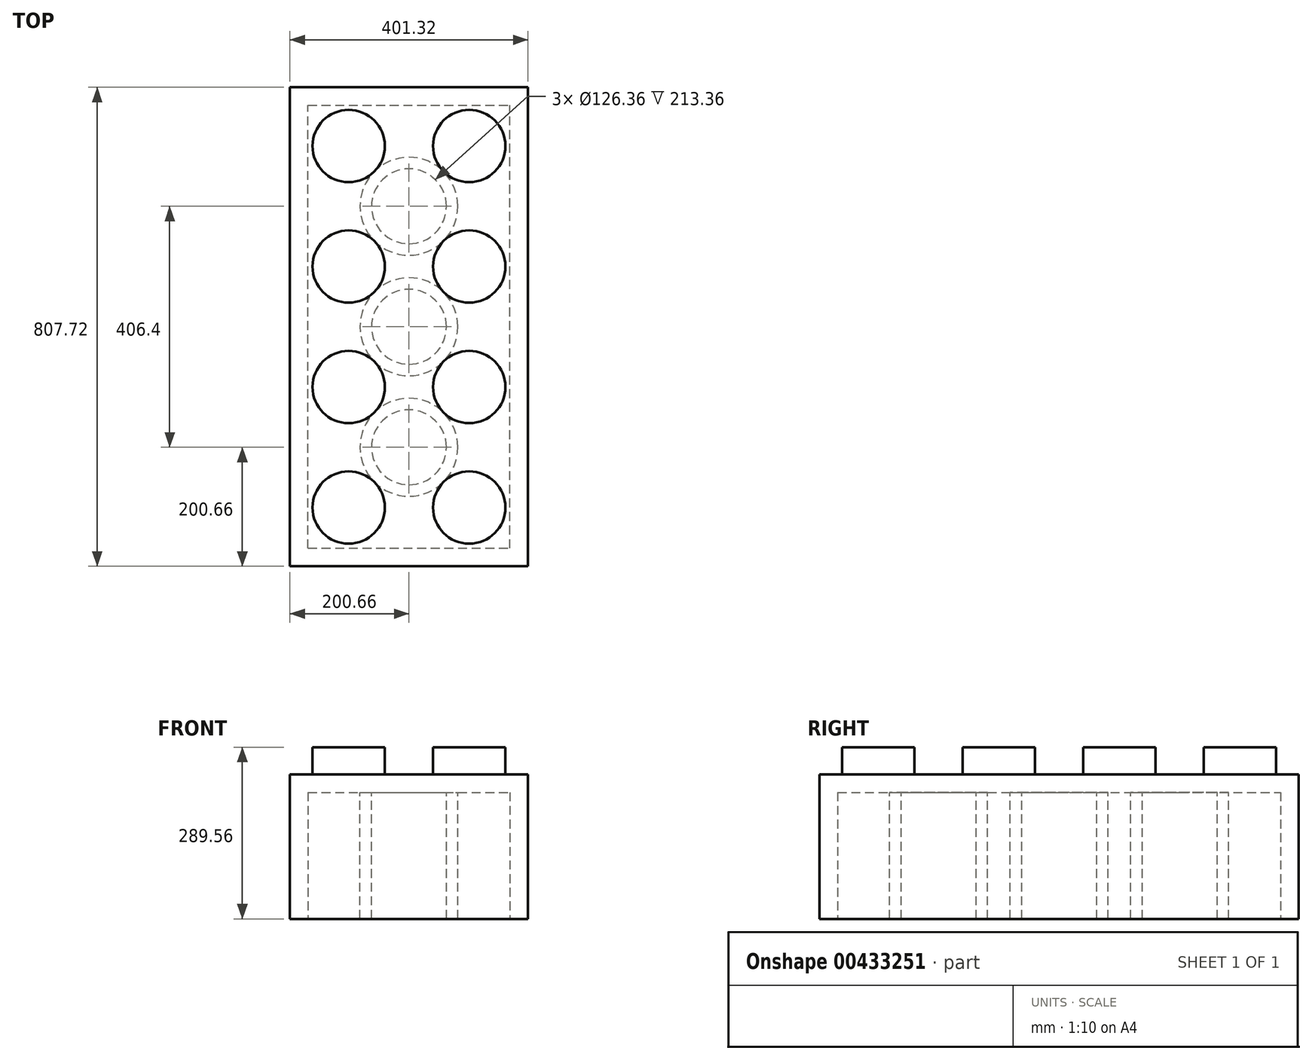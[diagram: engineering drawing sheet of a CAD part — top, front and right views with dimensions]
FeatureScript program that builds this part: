
annotation { "Feature Type Name" : "Feature", "Feature Type Description" : "" }
export const myFeature = defineFeature(function(context is Context, id is Id, definition is map)
    precondition{}
    {
        {
            var Q0;
            Q0=qCreatedBy(makeId("Top.planeOp"),FACE);
            var sketch = newSketch(context, id + "F0", { "sketchPlane" : qUnion([Q0])});
            skLineSegment(sketch, "E0.bottom", {"start": v(-200.66, -403.86) * mm, "end": v(200.66, -403.86) * mm});
            skLineSegment(sketch, "E0.top", {"start": v(-200.66, 403.86) * mm, "end": v(200.66, 403.86) * mm});
            skLineSegment(sketch, "E0.left", {"start": v(-200.66, -403.86) * mm, "end": v(-200.66, 403.86) * mm});
            skLineSegment(sketch, "E0.right", {"start": v(200.66, -403.86) * mm, "end": v(200.66, 403.86) * mm});
            skPoint(sketch, "E0.middle", {"position": v(0, 0) * mm});
            skSolve(sketch);
        }
        {
            var Q0;
            Q0=qSketchRegion(id+"F0",true);
            extrude(context, id + "F1", {"entities" : qUnion([Q0]), "depth" : 243.84 * mm});
        }
        {
            var Q0;
            Q0=makeQuery(id+"F1.opExtrude","CAP_FACE",FACE,{"disambiguationData":[OSD([sQuery(id+"F0.wireOp",EDGE,"E0.bottom"),sQuery(id+"F0.wireOp",EDGE,"E0.top"),sQuery(id+"F0.wireOp",EDGE,"E0.left"),sQuery(id+"F0.wireOp",EDGE,"E0.right")])],"isStart":false});
            var sketch = newSketch(context, id + "F2", { "sketchPlane" : qUnion([Q0])});
            skCircle(sketch, "E1", {"center": v(101.6, 304.8) * mm, "radius": 60.96 * mm});
            skCircle(sketch, "E2.0.1.0", {"center": v(101.6, 101.6) * mm, "radius": 60.96 * mm});
            skCircle(sketch, "E2.0.2.0", {"center": v(101.6, -101.6) * mm, "radius": 60.96 * mm});
            skCircle(sketch, "E2.0.3.0", {"center": v(101.6, -304.8) * mm, "radius": 60.96 * mm});
            skCircle(sketch, "E2.1.0.0", {"center": v(-101.6, 304.8) * mm, "radius": 60.96 * mm});
            skCircle(sketch, "E2.1.1.0", {"center": v(-101.6, 101.6) * mm, "radius": 60.96 * mm});
            skCircle(sketch, "E2.1.2.0", {"center": v(-101.6, -101.6) * mm, "radius": 60.96 * mm});
            skCircle(sketch, "E2.1.3.0", {"center": v(-101.6, -304.8) * mm, "radius": 60.96 * mm});
            skLineSegment(sketch, "E2.direction1", {"start": v(101.6, 304.8) * mm, "end": v(-101.6, 304.8) * mm, "construction": true});
            skLineSegment(sketch, "E2.direction2", {"start": v(101.6, 304.8) * mm, "end": v(101.6, 101.6) * mm, "construction": true});
            skSolve(sketch);
        }
        {
            var Q0;
            Q0=qSketchRegion(id+"F2",true);
            extrude(context, id + "F3", {"entities" : qUnion([Q0]), "operationType" : NewBodyOperationType.ADD, "depth" : 45.72 * mm});
        }
        {
            var Q0;
            Q0=makeQuery(id+"F1.opExtrude","CAP_FACE",FACE,{"disambiguationData":[OSD([sQuery(id+"F0.wireOp",EDGE,"E0.bottom"),sQuery(id+"F0.wireOp",EDGE,"E0.top"),sQuery(id+"F0.wireOp",EDGE,"E0.left"),sQuery(id+"F0.wireOp",EDGE,"E0.right")])],"isStart":true});
            var sketch = newSketch(context, id + "F4", { "sketchPlane" : qUnion([Q0])});
            skLineSegment(sketch, "E3.bottom", {"start": v(-170.18, 373.38) * mm, "end": v(170.18, 373.38) * mm});
            skLineSegment(sketch, "E3.top", {"start": v(-170.18, -373.38) * mm, "end": v(170.18, -373.38) * mm});
            skLineSegment(sketch, "E3.left", {"start": v(-170.18, 373.38) * mm, "end": v(-170.18, -373.38) * mm});
            skLineSegment(sketch, "E3.right", {"start": v(170.18, 373.38) * mm, "end": v(170.18, -373.38) * mm});
            skPoint(sketch, "E3.middle", {"position": v(0, 0) * mm});
            skSolve(sketch);
        }
        {
            var Q0;
            Q0=makeQuery(id+"F4.imprint","IMPRINT",FACE,{"disambiguationData":[TD([[makeQuery(id+"F4.imprint","IMPRINT",EDGE,{"derivedFrom":sQuery(id+"F4.wireOp",EDGE,"E3.bottom")}),-1.0]])]});
            extrude(context, id + "F5", {"entities" : qUnion([Q0]), "operationType" : NewBodyOperationType.REMOVE, "oppositeDirection" : true, "depth" : 213.36 * mm});
        }
        {
            var Q0;
            Q0=makeQuery(id+"F5.boolean.opBoolean","COPY",FACE,{"derivedFrom":makeQuery(id+"F5.opExtrude","CAP_FACE",FACE,{"disambiguationData":[OSD([sQuery(id+"F4.wireOp",EDGE,"E3.bottom"),sQuery(id+"F4.wireOp",EDGE,"E3.top"),sQuery(id+"F4.wireOp",EDGE,"E3.left"),sQuery(id+"F4.wireOp",EDGE,"E3.right")])],"isStart":false})});
            var sketch = newSketch(context, id + "F6", { "sketchPlane" : qUnion([Q0])});
            skCircle(sketch, "E4", {"center": v(0, 0) * mm, "radius": 82.55 * mm});
            skCircle(sketch, "E5", {"center": v(0, 0) * mm, "radius": 63.18 * mm});
            skCircle(sketch, "E6.0.1.0", {"center": v(0, 203.2) * mm, "radius": 82.55 * mm});
            skLineSegment(sketch, "E6.direction1", {"start": v(0, 0) * mm, "end": v(25.4, 0) * mm, "construction": true});
            skLineSegment(sketch, "E6.direction2", {"start": v(0, 0) * mm, "end": v(0, 203.2) * mm, "construction": true});
            skCircle(sketch, "E7.0.1.0", {"center": v(0, 203.2) * mm, "radius": 63.18 * mm});
            skCircle(sketch, "E8.0.1.0", {"center": v(0, -203.2) * mm, "radius": 63.18 * mm});
            skCircle(sketch, "E8.0.1.1", {"center": v(0, -203.2) * mm, "radius": 82.55 * mm});
            skLineSegment(sketch, "E8.direction1", {"start": v(0, 203.2) * mm, "end": v(25.4, 203.2) * mm, "construction": true});
            skLineSegment(sketch, "E8.direction2", {"start": v(0, 203.2) * mm, "end": v(0, -203.2) * mm, "construction": true});
            skSolve(sketch);
        }
        {
            var Q0;
            Q0=qSketchRegion(id+"F6",true);
            var Q1;
            Q1=sQuery(id+"F6.wireOp",EDGE,"E6.0.1.0");
            var Q2;
            Q2=sQuery(id+"F6.wireOp",EDGE,"E7.0.1.0");
            var Q3;
            Q3=sQuery(id+"F6.wireOp",EDGE,"E5");
            var Q4;
            Q4=sQuery(id+"F6.wireOp",EDGE,"E4");
            var Q5;
            Q5=sQuery(id+"F6.wireOp",EDGE,"E8.0.1.0");
            var Q6;
            Q6=sQuery(id+"F6.wireOp",EDGE,"E8.0.1.1");
            extrude(context, id + "F7", {"entities" : qUnion([Q0]), "operationType" : NewBodyOperationType.ADD, "surfaceEntities" : qUnion([Q1, Q2, Q3, Q4, Q5, Q6]), "depth" : 213.36 * mm});
        }
    });
